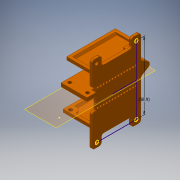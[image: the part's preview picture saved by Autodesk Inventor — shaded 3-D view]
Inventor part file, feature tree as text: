
AUTODESK INVENTOR PART (.ipt)
format: ipt  version: 2017 (Build 210142000, 142)  size: 472,064 bytes
history: native  units: mm
features: extrude x13, sketch x13, other x8, reference x7, projected_geometry x5, chamfer x3, fillet x1
ambient origin geometry x8: Origin, YZ Plane, XZ Plane, XY Plane, X Axis, Y Axis, Z Axis, Center Point
bodies: Solid1 (feature_tree)
feature tree (50):
  extrude  "Extrusion1"  Depth=54.0mm
  extrude  "Extrusion2"  Depth=3.5mm
  extrude  "Extrusion3"  Depth=3.5mm
  chamfer  "Chamfer1"  Distance=150.0mm
  chamfer  "Chamfer2"  Distance=10.0mm
  extrude  "Extrusion4"  Depth=17.9mm
  extrude  "Extrusion5"  Depth=5.0mm
  extrude  "Extrusion6"  Depth=2.0mm TaperAngle=45.0deg
  extrude  "Extrusion7"  Depth=2.0mm
  extrude  "Extrusion8"  Depth=20.0mm
  extrude  "Extrusion9"  Depth=20.0mm
  extrude  "Extrusion10"  Depth=23.0mm
  extrude  "Extrusion11"  Depth=9.75mm
  extrude  "Extrusion12"  Depth=58.9mm
  extrude  "Extrusion13"  Depth=58.9mm
  chamfer  "Chamfer3"  Distance=3.3mm
  fillet  "Fillet1"  Radius=3.3mm
  other  "measure and reference"
  other  "midplane"
  sketch  "Sketch1"  dims[d0=3.0mm d1=0.0mm d3=54.0mm]
  reference  "Reference1"
  reference  "Reference2"
  reference  "Reference3"
  sketch  "Sketch2"  dims[d4=3.5mm d5=4.0mm]
  reference  "Reference4"
  reference  "Reference5"
  reference  "Reference6"
  sketch  "Sketch3"  dims[d6=3.5mm d7=1.75mm]
  sketch  "Sketch4"  dims[d8=2.54mm d9=150.0mm d11=2.54mm d12=10.0mm d14=10.0mm]
  projected_geometry  "Projected Loop1"
  reference  "Reference7"
  sketch  "Sketch5"  dims[d16=17.9mm d17=43.7mm]
  sketch  "Sketch6"  dims[d18=2.0mm d19=0.0mm d20=5.0mm]
  sketch  "Sketch7"  dims[d21=2.0mm d22=0.0mm d23=2.0mm d24=2.0mm d25=45.0deg]
  sketch  "Sketch8"  dims[d26=2.0mm d27=2.0mm d28=45.0deg d29=2.0mm]
  sketch  "Sketch9"  dims[d30=2.0mm d31=0.0mm d32=20.0mm]
  sketch  "Sketch10"  dims[d33=13.0mm d34=20.0mm]
  projected_geometry  "Projected Loop2"
  projected_geometry  "Projected Loop3"
  sketch  "Sketch11"  dims[d35=2.5mm d36=23.0mm]
  sketch  "Sketch12"  dims[d37=2.5mm d38=9.75mm]
  projected_geometry  "Projected Loop4"
  sketch  "Sketch13"  dims[d39=42.0mm d40=0.0mm d41=16.0mm d42=30.4mm d43=3.3mm d44=3.3mm d45=3.0mm d46=0.0mm d47=9.0mm d48=3.75mm d49=10.0mm d50=5.0mm d51=2.0mm d52=0.0mm d53=12.0mm d55=2.0mm d56=0.0mm d57=2.0mm d58=8.0mm d59=8.0mm d60=0.0mm d61=8.0mm d62=0.0mm d63=3.0mm d64=8.0mm d65=0.0mm d66=2.5mm d67=1.5mm d68=0.0mm d69=2.5mm d70=3.0mm d71=3.0mm d72=1.5mm d73=0.0mm d74=1.5mm d75=2.0mm d76=45.0deg d77=58.9mm]
  projected_geometry  "Projected Loop5"
  parser-record x1  (decoder bookkeeping rows leaked as tree rows — omitted from the tree; the rows remain in map.json)
  other  "Ganymede Node.iam"
  other  "moist probe:1"
  other  "soil sensor:1"
  other  "NanoV3 v4:1"
  other  "NRF24L01+:1"
note: 1 file-system path scrubbed to <path> (originals preserved in map.json)
